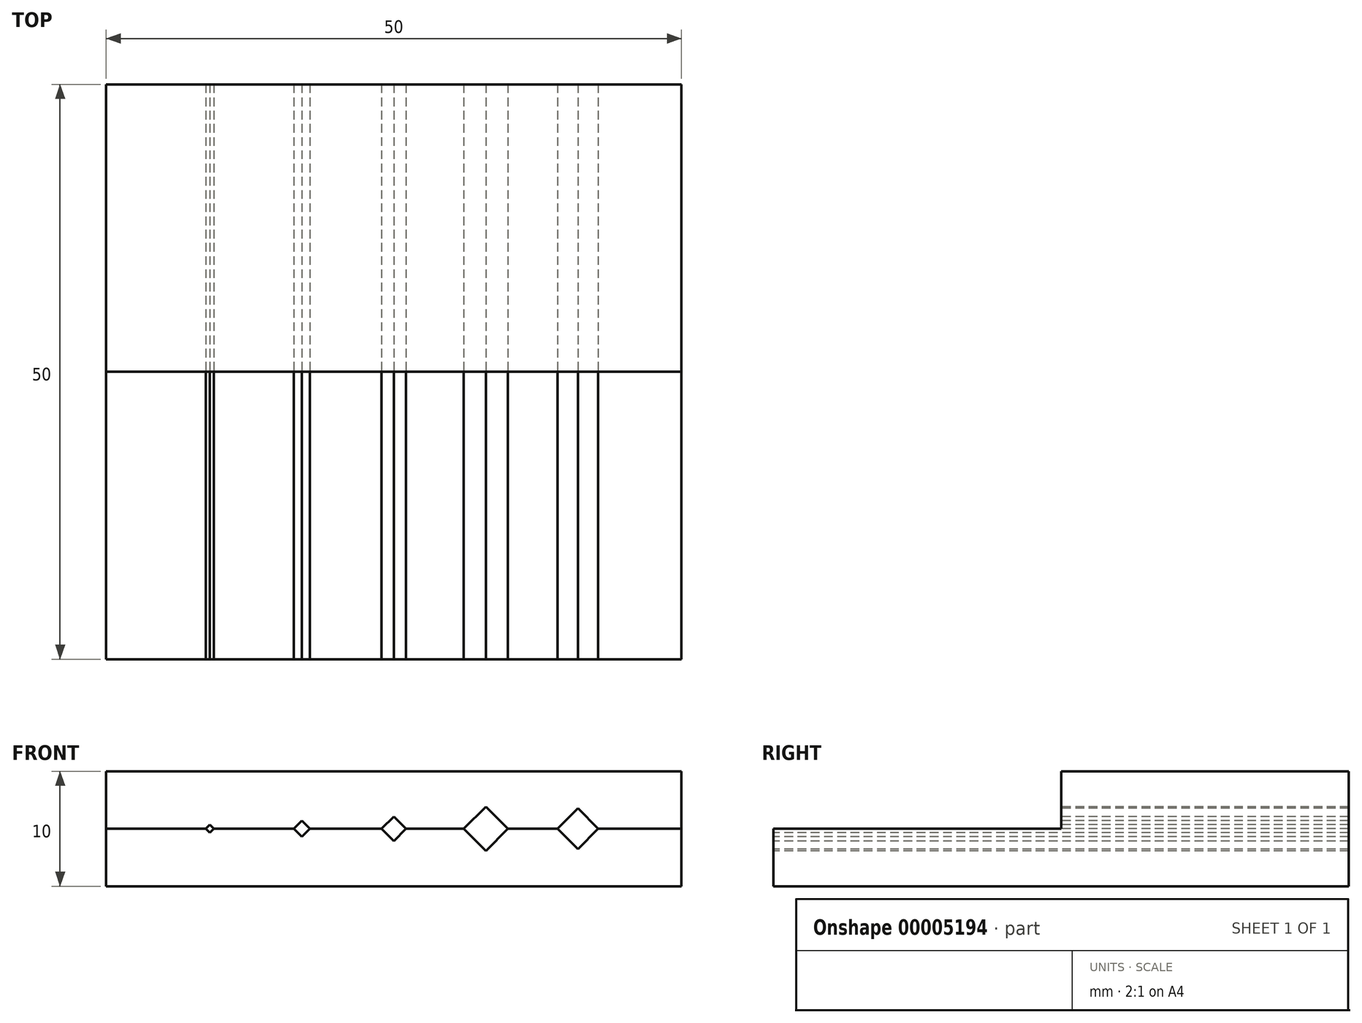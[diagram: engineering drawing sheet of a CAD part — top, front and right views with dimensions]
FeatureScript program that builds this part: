
annotation { "Feature Type Name" : "Feature", "Feature Type Description" : "" }
export const myFeature = defineFeature(function(context is Context, id is Id, definition is map)
    precondition{}
    {
        {
            var Q0;
            Q0=qCreatedBy(makeId("Top.planeOp"),FACE);
            var sketch = newSketch(context, id + "F0", { "sketchPlane" : qUnion([Q0])});
            skLineSegment(sketch, "E0.rect.bottom", {"start": v(25, 25) * mm, "end": v(-25, 25) * mm});
            skLineSegment(sketch, "E0.rect.top", {"start": v(25, -25) * mm, "end": v(-25, -25) * mm});
            skLineSegment(sketch, "E0.rect.left", {"start": v(25, 25) * mm, "end": v(25, -25) * mm});
            skLineSegment(sketch, "E0.rect.right", {"start": v(-25, 25) * mm, "end": v(-25, -25) * mm});
            skPoint(sketch, "E0.rect.middle", {"position": v(0, 0) * mm});
            skSolve(sketch);
        }
        {
            var Q0;
            Q0=qSketchRegion(id+"F0",true);
            extrude(context, id + "F1", {"entities" : qUnion([Q0]), "depth" : 10 * mm});
        }
        {
            var Q0;
            Q0=makeQuery(id+"F1.opExtrude","SWEPT_FACE",FACE,{"disambiguationData":[OSD([sQuery(id+"F0.wireOp",EDGE,"E0.rect.top")])]});
            var sketch = newSketch(context, id + "F2", { "sketchPlane" : qUnion([Q0])});
            skLineSegment(sketch, "E1", {"start": v(-25, 5) * mm, "end": v(25, 5) * mm, "construction": true});
            skPoint(sketch, "E2.rect.middle", {"position": v(-16, 5) * mm});
            skCircle(sketch, "E3.cCircle", {"center": v(-16, 5) * mm, "radius": 0.25 * mm, "construction": true});
            skLineSegment(sketch, "E3.0", {"start": v(-16, 5.35) * mm, "end": v(-15.65, 5) * mm});
            skLineSegment(sketch, "E3.1", {"start": v(-15.65, 5) * mm, "end": v(-16, 4.65) * mm});
            skLineSegment(sketch, "E3.2", {"start": v(-16, 4.65) * mm, "end": v(-16.35, 5) * mm});
            skLineSegment(sketch, "E3.3", {"start": v(-16.35, 5) * mm, "end": v(-16, 5.35) * mm});
            skPoint(sketch, "E3.0.midPoint", {"position": v(-15.82, 5.18) * mm});
            skCircle(sketch, "E4.cCircle", {"center": v(0, 5) * mm, "radius": 0.75 * mm, "construction": true});
            skLineSegment(sketch, "E4.0", {"start": v(0, 6.06) * mm, "end": v(1.06, 5) * mm});
            skLineSegment(sketch, "E4.1", {"start": v(1.06, 5) * mm, "end": v(0, 3.94) * mm});
            skLineSegment(sketch, "E4.2", {"start": v(0, 3.94) * mm, "end": v(-1.06, 5) * mm});
            skLineSegment(sketch, "E4.3", {"start": v(-1.06, 5) * mm, "end": v(0, 6.06) * mm});
            skPoint(sketch, "E4.0.midPoint", {"position": v(0.53, 5.53) * mm});
            skCircle(sketch, "E5.cCircle", {"center": v(-8, 5) * mm, "radius": 0.5 * mm, "construction": true});
            skLineSegment(sketch, "E5.0", {"start": v(-8, 5.7) * mm, "end": v(-7.3, 5) * mm});
            skLineSegment(sketch, "E5.1", {"start": v(-7.3, 5) * mm, "end": v(-8, 4.3) * mm});
            skLineSegment(sketch, "E5.2", {"start": v(-8, 4.3) * mm, "end": v(-8.7, 5) * mm});
            skLineSegment(sketch, "E5.3", {"start": v(-8.7, 5) * mm, "end": v(-8, 5.7) * mm});
            skPoint(sketch, "E5.0.midPoint", {"position": v(-7.65, 5.35) * mm});
            skCircle(sketch, "E6.cCircle", {"center": v(8, 5) * mm, "radius": 1.36 * mm, "construction": true});
            skLineSegment(sketch, "E6.0", {"start": v(8, 6.92) * mm, "end": v(9.92, 5) * mm});
            skLineSegment(sketch, "E6.1", {"start": v(9.92, 5) * mm, "end": v(8, 3.08) * mm});
            skLineSegment(sketch, "E6.2", {"start": v(8, 3.08) * mm, "end": v(6.08, 5) * mm});
            skLineSegment(sketch, "E6.3", {"start": v(6.08, 5) * mm, "end": v(8, 6.92) * mm});
            skPoint(sketch, "E6.0.midPoint", {"position": v(8.96, 5.96) * mm});
            skCircle(sketch, "E7.cCircle", {"center": v(16, 5) * mm, "radius": 1.25 * mm, "construction": true});
            skLineSegment(sketch, "E7.0", {"start": v(16, 6.77) * mm, "end": v(17.77, 5) * mm});
            skLineSegment(sketch, "E7.1", {"start": v(17.77, 5) * mm, "end": v(16, 3.23) * mm});
            skLineSegment(sketch, "E7.2", {"start": v(16, 3.23) * mm, "end": v(14.23, 5) * mm});
            skLineSegment(sketch, "E7.3", {"start": v(14.23, 5) * mm, "end": v(16, 6.77) * mm});
            skPoint(sketch, "E7.0.midPoint", {"position": v(16.88, 5.88) * mm});
            skSolve(sketch);
        }
        {
            var Q0;
            Q0=qSketchRegion(id+"F2",true);
            extrude(context, id + "F3", {"entities" : qUnion([Q0]), "operationType" : NewBodyOperationType.REMOVE, "endBound" : BoundingType.THROUGH_ALL, "oppositeDirection" : true, "depth" : 25 * mm});
        }
        {
            var Q0;
            Q0=makeQuery(id+"F1.opExtrude","SWEPT_FACE",FACE,{"disambiguationData":[OSD([sQuery(id+"F0.wireOp",EDGE,"E0.rect.top")])]});
            var sketch = newSketch(context, id + "F4", { "sketchPlane" : qUnion([Q0])});
            skLineSegment(sketch, "E8.bottom", {"start": v(-25, 10) * mm, "end": v(25, 10) * mm});
            skLineSegment(sketch, "E8.top", {"start": v(-25, 5) * mm, "end": v(25, 5) * mm});
            skLineSegment(sketch, "E8.left", {"start": v(-25, 10) * mm, "end": v(-25, 5) * mm});
            skLineSegment(sketch, "E8.right", {"start": v(25, 10) * mm, "end": v(25, 5) * mm});
            skSolve(sketch);
        }
        {
            var Q0;
            Q0=qSketchRegion(id+"F4",true);
            extrude(context, id + "F5", {"entities" : qUnion([Q0]), "operationType" : NewBodyOperationType.REMOVE, "oppositeDirection" : true, "depth" : 25 * mm});
        }
    });
